# Revit family: CIRS
name_source: partatom
category: Lighting Fixtures
revit_build: Autodesk Revit 2014 (Build: 20130308_1515(x64)
units: mm (PartAtom-declared; Revit-internal decimal feet)

## types (1)
- CIRS
    Apparent Load = 1 VA
    Body = Paint - Hubbell - Matte White
    Certification = UL924
    Color Filter = 16777215
    Default Elevation = 48 "
    Description = The Round Wall Forms luminaires include five configurations to suit any building application. The classic spherical shape and cross bar design have become an icon in outdoor lighting. An ADA compliant cutoff downlight design provides perimeter lighting while enhancing architecture.
    Dimming Lamp Color Temperature Shift = <None>
    Emit Shape Visible in Rendering = No
    Emit from Circle Diameter = 3 "
    Features = Single or Double, white or black lamp-head
remote with base-plate
• LED life-cycle of more than 10 years
• Quick installation
• Damp Location Listed
• Fully adjustable lamp-heads
    Glass = Glass - Hubbell - White
    Lamp = LED
    Manufacturer = Compass Lighting A unit of Hubbell Lighting
    Model = CIRS
    Photometric Note = For more photometric file please find the above link
    Photometric Web File = compass_led.ies
    Photometric Web Link = https://www.hubbell.com
    Product Doucumentation Link = https://hubbellcdn.com
    Product Page URL = https://www.hubbell.com
    Steel = Metal-Hubbell-Galvanized_Steel
    Tilt Angle = 0.00°
    Type Comments = Light Fixture
    URL = https://www.hubbell.com
    Warranty = 2 year full unit warranty
    Wattage Comments = 1W

## geometry (parser evidence)
native form markers: Sweep x3
no freeform markers — native parametric forms only
